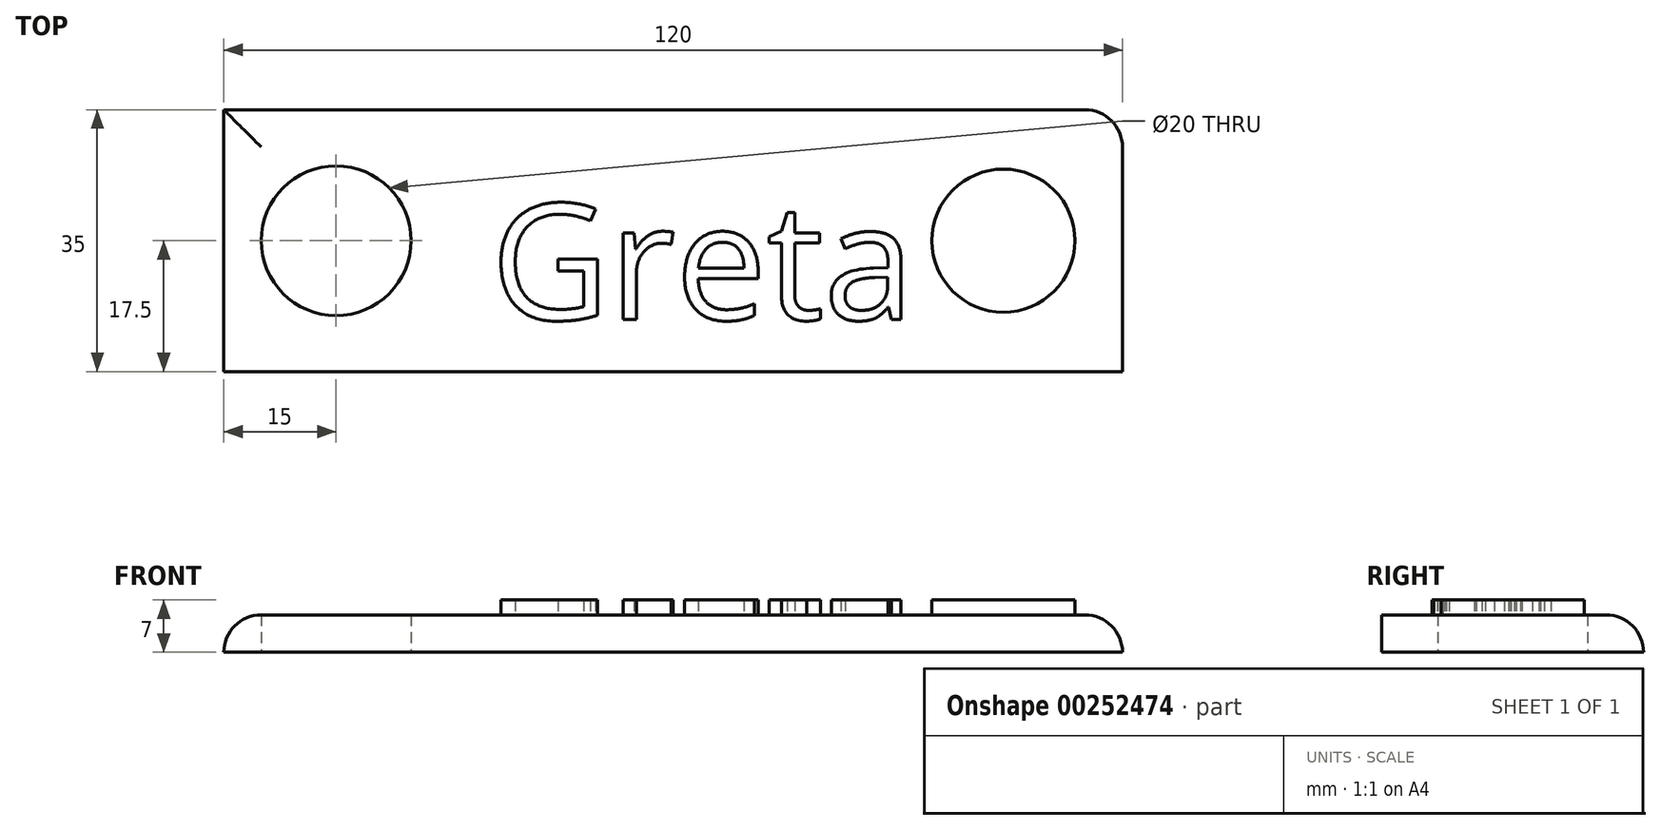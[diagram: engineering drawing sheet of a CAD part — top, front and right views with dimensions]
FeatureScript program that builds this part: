
annotation { "Feature Type Name" : "Feature", "Feature Type Description" : "" }
export const myFeature = defineFeature(function(context is Context, id is Id, definition is map)
    precondition{}
    {
        {
            var Q0;
            Q0=qCreatedBy(makeId("Top.planeOp"),FACE);
            var sketch = newSketch(context, id + "F0", { "sketchPlane" : qUnion([Q0])});
            skLineSegment(sketch, "E0.bottom", {"start": v(-60, 17.5) * mm, "end": v(60, 17.5) * mm});
            skLineSegment(sketch, "E0.top", {"start": v(-60, -17.5) * mm, "end": v(60, -17.5) * mm});
            skLineSegment(sketch, "E0.left", {"start": v(-60, 17.5) * mm, "end": v(-60, -17.5) * mm});
            skLineSegment(sketch, "E0.right", {"start": v(60, 17.5) * mm, "end": v(60, -17.5) * mm});
            skPoint(sketch, "E0.middle", {"position": v(0, 0) * mm});
            skCircle(sketch, "E1", {"center": v(-45, 0) * mm, "radius": 10 * mm});
            skSolve(sketch);
        }
        {
            var Q0;
            Q0=makeQuery(id+"F0.imprint","IMPRINT",FACE,{"disambiguationData":[TD([[makeQuery(id+"F0.imprint","IMPRINT",EDGE,{"derivedFrom":sQuery(id+"F0.wireOp",EDGE,"E0.bottom")}),-1.0]])]});
            extrude(context, id + "F1", {"entities" : qUnion([Q0]), "depth" : 5 * mm});
        }
        {
            var Q0;
            Q0=makeQuery(id+"F1.opExtrude","CAP_EDGE",EDGE,{"disambiguationData":[OSD([sQuery(id+"F0.wireOp",EDGE,"E0.left")])],"isStart":false});
            var Q1;
            Q1=makeQuery(id+"F1.opExtrude","CAP_EDGE",EDGE,{"disambiguationData":[OSD([sQuery(id+"F0.wireOp",EDGE,"E0.bottom")])],"isStart":false});
            fillet(context, id + "F2", {"entities" : qUnion([Q0, Q1]), "radius" : 5 * mm, "tangentPropagation" : true, "allowEdgeOverflow" : false});
        }
        {
            var Q0;
            Q0=makeQuery(id+"F1.opExtrude","CAP_EDGE",EDGE,{"disambiguationData":[OSD([sQuery(id+"F0.wireOp",EDGE,"E0.right")])],"isStart":false});
            fillet(context, id + "F3", {"entities" : qUnion([Q0]), "radius" : 5 * mm, "tangentPropagation" : true, "allowEdgeOverflow" : false});
        }
        {
            var Q0;
            Q0=makeQuery(id+"F1.opExtrude","CAP_FACE",FACE,{"disambiguationData":[OSD([sQuery(id+"F0.wireOp",EDGE,"E0.bottom"),sQuery(id+"F0.wireOp",EDGE,"E0.top"),sQuery(id+"F0.wireOp",EDGE,"E0.left"),sQuery(id+"F0.wireOp",EDGE,"E0.right"),sQuery(id+"F0.wireOp",EDGE,"E1")])],"isStart":false});
            var sketch = newSketch(context, id + "F4", { "sketchPlane" : qUnion([Q0])});
            skText(sketch, "E2", { "text": "Greta", "fontName": "OpenSans-Regular.ttf"});
            const initialGuessF4  = {"E2": [-0.0243, -0.01055, 1, 0, 0.0156]};
            skSetInitialGuess(sketch, initialGuessF4);
            skSolve(sketch);
        }
        {
            var Q0;
            Q0 = qSketchRegion(id + "F4", true);
            extrude(context, id + "F5", {"entities" : qUnion([Q0]), "operationType" : NewBodyOperationType.ADD, "depth" : 2 * mm});
        }
        {
            var Q0;
            {var subQ0=sQuery(id+"F0.wireOp",EDGE,"E1");var subQ1=sQuery(id+"F0.wireOp",EDGE,"E0.bottom");var subQ2=sQuery(id+"F0.wireOp",EDGE,"E0.top");var subQ3=sQuery(id+"F0.wireOp",EDGE,"E0.left");var subQ4=sQuery(id+"F0.wireOp",EDGE,"E0.right");Q0=makeQuery(id+"F5.boolean.opBoolean","SPLIT",FACE,{"disambiguationData":[TD([makeQuery(id+"F1.opExtrude","SWEPT_FACE",FACE,{"disambiguationData":[OSD([subQ2])]})])],"derivedFrom":makeQuery(id+"F1.opExtrude","CAP_FACE",FACE,{"disambiguationData":[OSD([subQ1,subQ2,subQ3,subQ4,subQ0])],"isStart":false})});}
            var sketch = newSketch(context, id + "F6", { "sketchPlane" : qUnion([Q0])});
            skCircle(sketch, "E3", {"center": v(44.11, 0) * mm, "radius": 9.56 * mm});
            skSolve(sketch);
        }
        {
            var Q0;
            Q0 = qSketchRegion(id + "F6", true);
            extrude(context, id + "F7", {"entities" : qUnion([Q0]), "operationType" : NewBodyOperationType.ADD, "depth" : 2 * mm});
        }
    });
